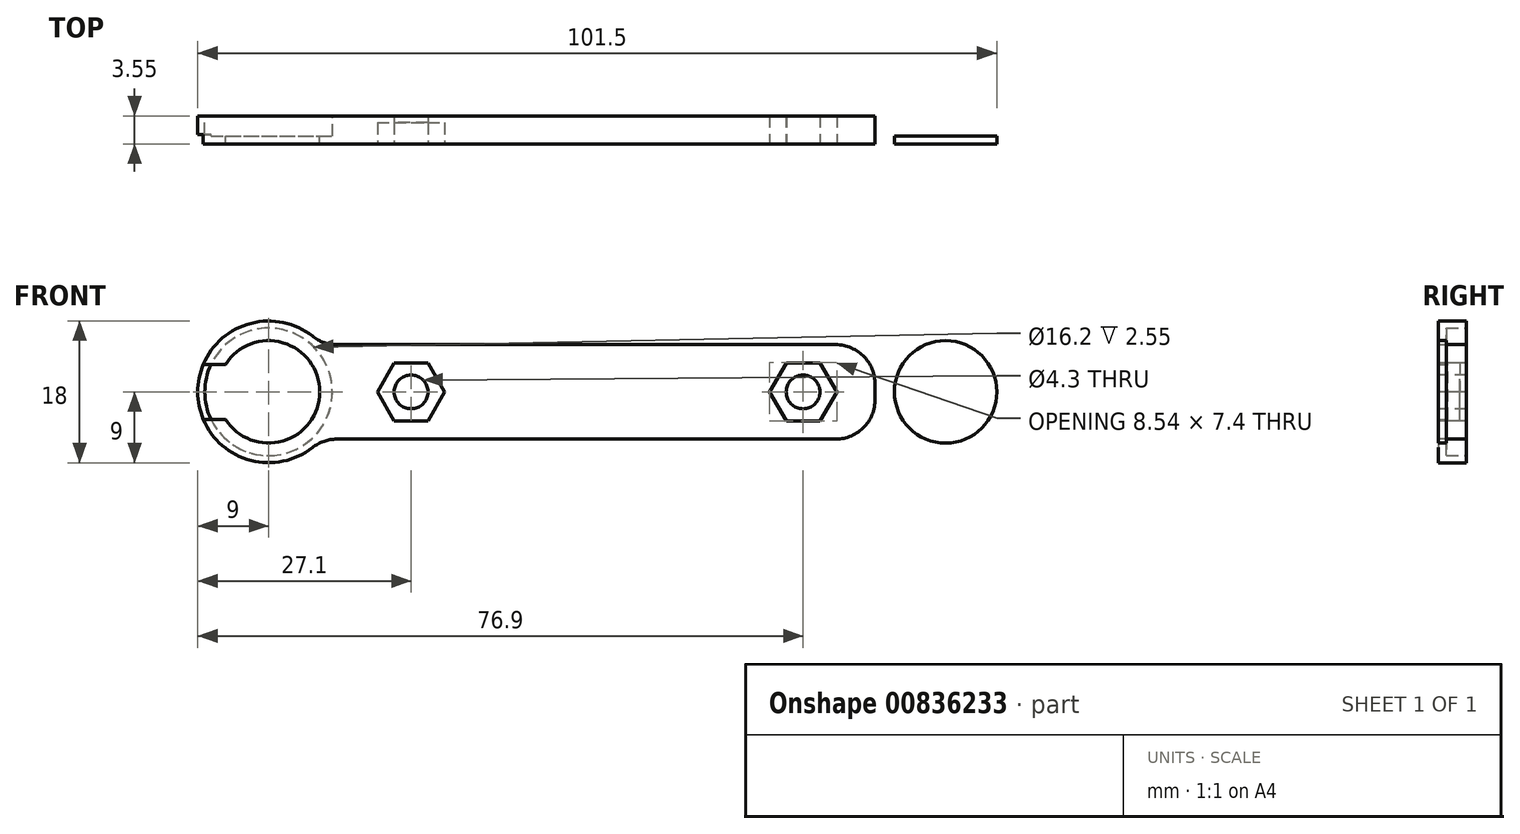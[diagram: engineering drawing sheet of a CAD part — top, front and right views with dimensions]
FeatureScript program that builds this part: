
annotation { "Feature Type Name" : "Feature", "Feature Type Description" : "" }
export const myFeature = defineFeature(function(context is Context, id is Id, definition is map)
    precondition{}
    {
        {
            var Q0;
            Q0=qCreatedBy(makeId("Front.planeOp"),FACE);
            var sketch = newSketch(context, id + "F0", { "sketchPlane" : qUnion([Q0])});
            skCircle(sketch, "E0", {"center": v(0, 0) * mm, "radius": 9 * mm});
            skLineSegment(sketch, "E1.bottom", {"start": v(0, 9) * mm, "end": v(86, 9) * mm});
            skLineSegment(sketch, "E1.top", {"start": v(0, -9) * mm, "end": v(86, -9) * mm});
            skLineSegment(sketch, "E1.left", {"start": v(0, 9) * mm, "end": v(0, -9) * mm});
            skLineSegment(sketch, "E1.right", {"start": v(86, 9) * mm, "end": v(86, -9) * mm});
            skLineSegment(sketch, "E2", {"start": v(43, 9) * mm, "end": v(43, -9) * mm, "construction": true});
            skCircle(sketch, "E3.MirrorC", {"center": v(86, 0) * mm, "radius": 9 * mm});
            skCircle(sketch, "E4", {"center": v(0, 0) * mm, "radius": 6.5 * mm});
            skCircle(sketch, "E5.MirrorC", {"center": v(86, 0) * mm, "radius": 6.5 * mm});
            skLineSegment(sketch, "E6", {"start": v(6.7, 6) * mm, "end": v(79.3, 6) * mm});
            skLineSegment(sketch, "E7.MirrorCS", {"start": v(6.7, -6) * mm, "end": v(79.3, -6) * mm});
            skSolve(sketch);
        }
        {
            var Q0;
            {var subQ0=sQuery(id+"F0.wireOp",EDGE,"E1.left");var subQ4=sQuery(id+"F0.wireOp",EDGE,"E4");var subQ5=makeQuery(id+"F0.imprint","INTERSECT",VERTEX,{"disambiguationData":[OD(0.0)],"derivedFrom":[subQ0,subQ4]});Q0=makeQuery(id+"F0.imprint","IMPRINT",FACE,{"disambiguationData":[TD([[makeQuery(id+"F0.imprint","IMPRINT",EDGE,{"disambiguationData":[TD([[subQ5,-1.0]])],"derivedFrom":subQ4}),-1.0]])]});}
            var Q1;
            {var subQ0=sQuery(id+"F0.wireOp",EDGE,"E1.left");var subQ4=sQuery(id+"F0.wireOp",EDGE,"E4");var subQ6=makeQuery(id+"F0.imprint","INTERSECT",VERTEX,{"disambiguationData":[OD(0.0)],"derivedFrom":[subQ0,subQ4]});Q1=makeQuery(id+"F0.imprint","IMPRINT",FACE,{"disambiguationData":[TD([[makeQuery(id+"F0.imprint","IMPRINT",EDGE,{"disambiguationData":[TD([[subQ6,1.0]])],"derivedFrom":subQ4}),-1.0]])]});}
            var Q2;
            {var subQ1=sQuery(id+"F0.wireOp",EDGE,"E1.right");var subQ3=sQuery(id+"F0.wireOp",EDGE,"E5.MirrorC");var subQ4=makeQuery(id+"F0.imprint","INTERSECT",VERTEX,{"disambiguationData":[OD(0.0)],"derivedFrom":[subQ1,subQ3]});Q2=makeQuery(id+"F0.imprint","IMPRINT",FACE,{"disambiguationData":[TD([[makeQuery(id+"F0.imprint","IMPRINT",EDGE,{"disambiguationData":[TD([[subQ4,1.0]])],"derivedFrom":subQ3}),1.0]])]});}
            var Q3;
            {var subQ1=sQuery(id+"F0.wireOp",EDGE,"E1.right");var subQ3=sQuery(id+"F0.wireOp",EDGE,"E5.MirrorC");var subQ4=makeQuery(id+"F0.imprint","INTERSECT",VERTEX,{"disambiguationData":[OD(0.0)],"derivedFrom":[subQ1,subQ3]});Q3=makeQuery(id+"F0.imprint","IMPRINT",FACE,{"disambiguationData":[TD([[makeQuery(id+"F0.imprint","IMPRINT",EDGE,{"disambiguationData":[TD([[subQ4,-1.0]])],"derivedFrom":subQ3}),1.0]])]});}
            var Q4;
            {var subQ0=sQuery(id+"F0.wireOp",EDGE,"E6");Q4=makeQuery(id+"F0.imprint","IMPRINT",FACE,{"disambiguationData":[TD([[makeQuery(id+"F0.imprint","IMPRINT",EDGE,{"derivedFrom":subQ0}),-1.0]])]});}
            var Q5;
            {var subQ1=sQuery(id+"F0.wireOp",EDGE,"gxhALLYT-9PyP-Ywsq-yYwQ-50HcdmkSMhOM");Q5=makeQuery(id+"F0.imprint","IMPRINT",FACE,{"disambiguationData":[TD([[makeQuery(id+"F0.imprint","IMPRINT",EDGE,{"derivedFrom":subQ1}),-1.0]])]});}
            var Q6;
            {var subQ0=sQuery(id+"F0.wireOp",EDGE,"c6fc8c3b-534b-4e0a-b437-16114844a2be0.MirrorCS");Q6=makeQuery(id+"F0.imprint","IMPRINT",FACE,{"disambiguationData":[TD([[makeQuery(id+"F0.imprint","IMPRINT",EDGE,{"derivedFrom":subQ0}),1.0]])]});}
            extrude(context, id + "F1", {"entities" : qUnion([Q0, Q1, Q2, Q3, Q4, Q5, Q6]), "depth" : 3.55 * mm, "offsetDistance" : 25 * mm});
        }
        {
            var Q0;
            {var subQ0=sQuery(id+"F0.wireOp",EDGE,"E4");var subQ1=sQuery(id+"F0.wireOp",EDGE,"E1.left");var subQ2=makeQuery(id+"F0.imprint","INTERSECT",VERTEX,{"disambiguationData":[OD(0.0)],"derivedFrom":[subQ1,subQ0]});Q0=makeQuery(id+"F0.imprint","IMPRINT",FACE,{"disambiguationData":[TD([[makeQuery(id+"F0.imprint","IMPRINT",EDGE,{"disambiguationData":[TD([[subQ2,-1.0]])],"derivedFrom":subQ1}),1.0]])]});}
            var sketch = newSketch(context, id + "F2", { "sketchPlane" : qUnion([Q0])});
            skCircle(sketch, "E8", {"center": v(0, 0) * mm, "radius": 8.1 * mm});
            skCircle(sketch, "E9.MirrorC", {"center": v(86, 0) * mm, "radius": 8.1 * mm});
            skSolve(sketch);
        }
        {
            var Q0;
            Q0 = qSketchRegion(id + "F2", true);
            extrude(context, id + "F3", {"entities" : qUnion([Q0]), "operationType" : NewBodyOperationType.REMOVE, "depth" : 2.55 * mm, "offsetDistance" : 25 * mm});
        }
        {
            var Q0;
            Q0=makeQuery(id+"F1.opExtrude","SWEPT_EDGE",EDGE,{"disambiguationData":[OSD([sQuery(id+"F0.wireOp",EDGE,"E0"),sQuery(id+"F0.wireOp",EDGE,"E7.MirrorCS")])]});
            var Q1;
            Q1=makeQuery(id+"F1.opExtrude","SWEPT_EDGE",EDGE,{"disambiguationData":[OSD([sQuery(id+"F0.wireOp",EDGE,"E0"),sQuery(id+"F0.wireOp",EDGE,"E6")])]});
            var Q2;
            Q2=makeQuery(id+"F1.opExtrude","SWEPT_EDGE",EDGE,{"disambiguationData":[OSD([sQuery(id+"F0.wireOp",EDGE,"E3.MirrorC"),sQuery(id+"F0.wireOp",EDGE,"E6")])]});
            var Q3;
            Q3=makeQuery(id+"F1.opExtrude","SWEPT_EDGE",EDGE,{"disambiguationData":[OSD([sQuery(id+"F0.wireOp",EDGE,"E3.MirrorC"),sQuery(id+"F0.wireOp",EDGE,"E7.MirrorCS")])]});
            fillet(context, id + "F4", {"entities" : qUnion([Q0, Q1, Q2, Q3]), "radius" : 5 * mm, "tangentPropagation" : true, "allowEdgeOverflow" : false});
        }
        {
            var Q0;
            Q0=makeQuery(id+"F1.opExtrude","CAP_FACE",FACE,{"disambiguationData":[OSD([sQuery(id+"F0.wireOp",EDGE,"E0"),sQuery(id+"F0.wireOp",EDGE,"E3.MirrorC"),sQuery(id+"F0.wireOp",EDGE,"E4"),sQuery(id+"F0.wireOp",EDGE,"E5.MirrorC"),sQuery(id+"F0.wireOp",EDGE,"E6"),sQuery(id+"F0.wireOp",EDGE,"E7.MirrorCS"),sQuery(id+"F0.wireOp",EDGE,"gxhALLYT-9PyP-Ywsq-yYwQ-50HcdmkSMhOM"),sQuery(id+"F0.wireOp",EDGE,"thVsnWnE-0hdv-SWO7-ve0O-bVwTQyIw6EyG"),sQuery(id+"F0.wireOp",EDGE,"mQasPrb5-rZVz-QQnG-qnkb-Z6DlfqKRHEtY"),sQuery(id+"F0.wireOp",EDGE,"c6fc8c3b-534b-4e0a-b437-16114844a2be0.MirrorCS"),sQuery(id+"F0.wireOp",EDGE,"ba5401c5-3092-44f3-98f8-ef93550902ab0.MirrorCS"),sQuery(id+"F0.wireOp",EDGE,"f847f72f-e32b-4d2e-8332-8ab1cd27103a0.MirrorCS"),sQuery(id+"F0.wireOp",EDGE,"e6a71848-205c-46f1-8698-975e024f9603.filletArc"),sQuery(id+"F0.wireOp",EDGE,"80e848d3-f4b7-49f5-a9a6-eedf33251102.filletArc"),sQuery(id+"F0.wireOp",EDGE,"e693dcfb-07d4-4cbb-b386-b27ba18bcf26.filletArc"),sQuery(id+"F0.wireOp",EDGE,"4b734153-b044-4dbb-95a8-831a4db44591.filletArc")])],"isStart":false});
            var sketch = newSketch(context, id + "F5", { "sketchPlane" : qUnion([Q0])});
            skCircle(sketch, "E10.cCircle", {"center": v(18.1, 0) * mm, "radius": 3.7 * mm, "construction": true});
            skLineSegment(sketch, "E10.0", {"start": v(20.24, 3.7) * mm, "end": v(22.37, 0) * mm});
            skLineSegment(sketch, "E10.1", {"start": v(22.37, 0) * mm, "end": v(20.24, -3.7) * mm});
            skLineSegment(sketch, "E10.2", {"start": v(20.24, -3.7) * mm, "end": v(15.96, -3.7) * mm});
            skLineSegment(sketch, "E10.3", {"start": v(15.96, -3.7) * mm, "end": v(13.83, 0) * mm});
            skLineSegment(sketch, "E10.4", {"start": v(13.83, 0) * mm, "end": v(15.96, 3.7) * mm});
            skLineSegment(sketch, "E10.5", {"start": v(15.96, 3.7) * mm, "end": v(20.24, 3.7) * mm});
            skPoint(sketch, "E10.0.midPoint", {"position": v(21.3, 1.85) * mm});
            skLineSegment(sketch, "E11.MirrorCS", {"start": v(65.76, -3.7) * mm, "end": v(70.04, -3.7) * mm});
            skLineSegment(sketch, "E12.MirrorCS", {"start": v(70.04, -3.7) * mm, "end": v(72.17, 0) * mm});
            skLineSegment(sketch, "E13.MirrorCS", {"start": v(72.17, 0) * mm, "end": v(70.04, 3.7) * mm});
            skLineSegment(sketch, "E14.MirrorCS", {"start": v(70.04, 3.7) * mm, "end": v(65.76, 3.7) * mm});
            skLineSegment(sketch, "E15.MirrorCS", {"start": v(65.76, 3.7) * mm, "end": v(63.63, 0) * mm});
            skLineSegment(sketch, "E16.MirrorCS", {"start": v(63.63, 0) * mm, "end": v(65.76, -3.7) * mm});
            skCircle(sketch, "E17", {"center": v(18.1, 0) * mm, "radius": 2.15 * mm});
            skCircle(sketch, "E18.MirrorC", {"center": v(67.9, 0) * mm, "radius": 2.15 * mm});
            skSolve(sketch);
        }
        {
            var Q0;
            Q0 = qSketchRegion(id + "F5", true);
            extrude(context, id + "F6", {"entities" : qUnion([Q0]), "operationType" : NewBodyOperationType.REMOVE, "oppositeDirection" : true, "depth" : 2.7 * mm, "offsetDistance" : 25 * mm});
        }
        {
            var Q0;
            Q0=makeQuery(id+"F5.imprint","IMPRINT",FACE,{"disambiguationData":[TD([[makeQuery(id+"F5.imprint","IMPRINT",EDGE,{"derivedFrom":sQuery(id+"F5.wireOp",EDGE,"E17")}),1.0]])]});
            var Q1;
            Q1=makeQuery(id+"F5.imprint","IMPRINT",FACE,{"disambiguationData":[TD([[makeQuery(id+"F5.imprint","IMPRINT",EDGE,{"derivedFrom":sQuery(id+"F5.wireOp",EDGE,"E18.MirrorC")}),-1.0]])]});
            extrude(context, id + "F7", {"entities" : qUnion([Q0, Q1]), "operationType" : NewBodyOperationType.REMOVE, "endBound" : BoundingType.THROUGH_ALL, "oppositeDirection" : true, "depth" : 25 * mm, "offsetDistance" : 25 * mm});
        }
        {
            var Q0;
            Q0=qCreatedBy(makeId("Right.planeOp"),FACE);
            var sketch = newSketch(context, id + "F8", { "sketchPlane" : qUnion([Q0])});
            skLineSegment(sketch, "E19.bottom", {"start": v(-3.55, -3.5) * mm, "end": v(-2.35, -3.5) * mm});
            skLineSegment(sketch, "E19.top", {"start": v(-3.55, 3.5) * mm, "end": v(-2.35, 3.5) * mm});
            skLineSegment(sketch, "E19.left", {"start": v(-3.55, -3.5) * mm, "end": v(-3.55, 3.5) * mm});
            skLineSegment(sketch, "E19.right", {"start": v(-2.35, -3.5) * mm, "end": v(-2.35, 3.5) * mm});
            skSolve(sketch);
        }
        {
            var Q0;
            Q0 = qSketchRegion(id + "F8", true);
            extrude(context, id + "F9", {"entities" : qUnion([Q0]), "operationType" : NewBodyOperationType.REMOVE, "oppositeDirection" : true, "depth" : 200 * mm, "offsetDistance" : 25 * mm});
        }
    });
